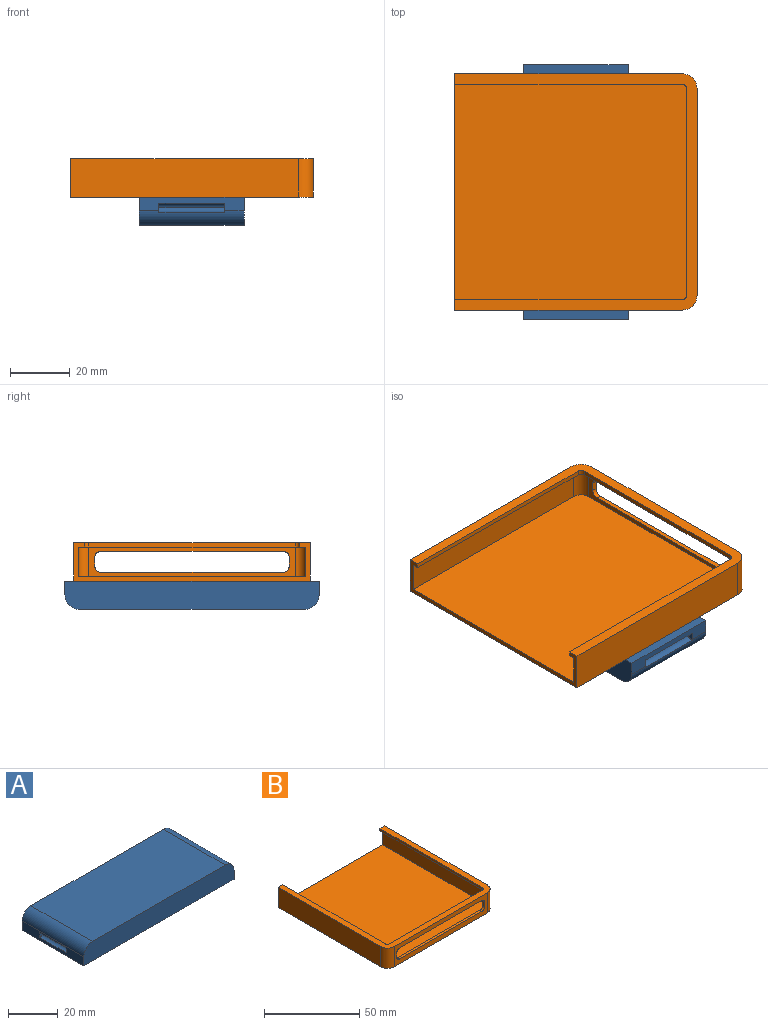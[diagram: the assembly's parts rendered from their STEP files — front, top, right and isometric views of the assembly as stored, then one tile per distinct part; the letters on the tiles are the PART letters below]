
ASSEMBLY  parts=2 mates=1
PART A: 16 faces, bbox 85x35x9.5 mm
  f0: cylinder r=5mm len=35mm, axis (0,-1,0), area 263.9mm2, adj f2,f3,f4,f5,f12,f13,f15
  f1: plane 35x4.5mm, normal (-1,0,0), area 123mm2, adj f2,f4,f6,f7,f8,f9,f10,f11
  f2: plane 85x9.5mm, normal (0,-1,0), area 796.8mm2, adj f0,f1,f3,f5,f6,f7
  f3: plane 35x4.5mm, normal (1,0,0), area 102.5mm2, adj f0,f2,f4,f6,f12,f13,f14
  f4: plane 85x9.5mm, normal (0,1,0), area 796.8mm2, adj f0,f1,f3,f5,f6,f7
  f5: plane 75x35mm, normal (0,0,1), area 2625mm2, adj f0,f2,f4,f7
  f6: plane 85x35mm, normal (0,0,-1), area 2975mm2, adj f1,f2,f3,f4
  f7: cylinder r=5mm len=35mm, axis (0,1,0), area 274.9mm2, adj f1,f2,f4,f5
  f8: plane 2.3x1.81mm, normal (0,-1,0), area 3mm2, adj f1,f10,f11
  f9: plane 2.3x1.81mm, normal (0,1,0), area 3mm2, adj f1,f10,f11
  f10: cylinder r=2mm len=15mm, axis (0,-1,0), area 34mm2, adj f1,f8,f9,f11
  f11: cylinder r=2mm len=15mm, axis (0,1,0), area 34mm2, adj f1,f8,f9,f10
  f12: plane 3x1.94mm, normal (0,1,0), area 4.3mm2, adj f0,f3,f14,f15
  f13: plane 3x1.94mm, normal (0,-1,0), area 4.3mm2, adj f0,f3,f14,f15
  f14: cylinder r=2mm len=22mm, axis (0,1,0), area 58mm2, adj f3,f12,f13,f15
  f15: cylinder r=2mm len=22mm, axis (0,-1,0), area 57.4mm2, adj f0,f12,f13,f14
PART B: 28 faces, bbox 79x81x12.9 mm
  f0: plane 69x12.9mm, normal (0,-1,0), area 438.5mm2, adj f6,f7,f8,f19,f20,f21,f22,f23
  f1: plane 69x9.9mm, normal (0,1,0), area 231.5mm2, adj f2,f11,f12,f13,f20,f21,f22,f23
  f2: plane 79.5x76mm, normal (0,0,1), area 6036.7mm2, adj f1,f3,f9,f10,f11,f12
  f3: plane 79x12.9mm, normal (0,1,0), area 158.7mm2, adj f2,f4,f5,f6,f9,f10,f13,f14
  f4: plane 76x12.9mm, normal (-1,0,0), area 980.4mm2, adj f3,f6,f7,f19
  f5: plane 76x12.9mm, normal (1,0,0), area 980.4mm2, adj f3,f6,f8,f19
  f6: plane 81x79mm, normal (0,0,-1), area 6388.3mm2, adj f0,f3,f4,f5,f7,f8
  f7: cylinder r=5mm len=12.9mm, axis (0,0,-1), area 101.3mm2, adj f0,f4,f6,f19
  f8: cylinder r=5mm len=12.9mm, axis (0,0,1), area 101.3mm2, adj f0,f5,f6,f19
  f9: plane 76x9.9mm, normal (1,0,0), area 752.4mm2, adj f2,f3,f12,f13
  f10: plane 76x9.9mm, normal (-1,0,0), area 752.4mm2, adj f2,f3,f11,f13
  f11: cylinder r=3.5mm len=9.9mm, axis (0,0,-1), area 54.4mm2, adj f1,f2,f10,f13
  f12: cylinder r=3.5mm len=9.9mm, axis (0,0,-1), area 54.4mm2, adj f1,f2,f9,f13
  f13: plane 79.5x76mm, normal (0,0,-1), area 457.7mm2, adj f1,f3,f9,f10,f11,f12,f14,f15
  f14: plane 76x1.5mm, normal (1,0,0), area 114mm2, adj f3,f13,f18,f19
  f15: plane 76x1.5mm, normal (-1,0,0), area 114mm2, adj f3,f13,f16,f19
  f16: cylinder r=1.5mm len=1.5mm, axis (0,0,-1), area 3.5mm2, adj f13,f15,f17,f19
  f17: plane 69x1.5mm, normal (0,1,0), area 103.5mm2, adj f13,f16,f18,f19
  f18: cylinder r=1.5mm len=1.5mm, axis (0,0,-1), area 3.5mm2, adj f13,f14,f17,f19
  f19: plane 81x79mm, normal (0,0,1), area 809.2mm2, adj f0,f3,f4,f5,f7,f8,f14,f15
  f20: plane 61x1.5mm, normal (0,0,-1), area 91.5mm2, adj f0,f1,f24,f27
  f21: plane 3x1.5mm, normal (-1,0,0), area 4.5mm2, adj f0,f1,f24,f25
  f22: plane 61x1.5mm, normal (0,0,1), area 91.5mm2, adj f0,f1,f25,f26
  f23: plane 3x1.5mm, normal (1,0,0), area 4.5mm2, adj f0,f1,f26,f27
  f24: cylinder r=2mm len=2mm, axis (0,1,0), area 4.7mm2, adj f0,f1,f20,f21
  f25: cylinder r=2mm len=2mm, axis (0,-1,0), area 4.7mm2, adj f0,f1,f21,f22
  f26: cylinder r=2mm len=2mm, axis (0,1,0), area 4.7mm2, adj f0,f1,f22,f23
  f27: cylinder r=2mm len=2mm, axis (0,-1,0), area 4.7mm2, adj f0,f1,f20,f23
PLACE A rot(axis=(0.71,-0.71,0),180deg) t=(10,-5.96,102.95)mm
PLACE B rot(axis=(0,0,1),90deg) t=(-30.44,-5.96,102.95)mm
MATE fastened A.f6 <-> B.f6  axis (0,0,1) through (10,-5.96,102.95)mm
